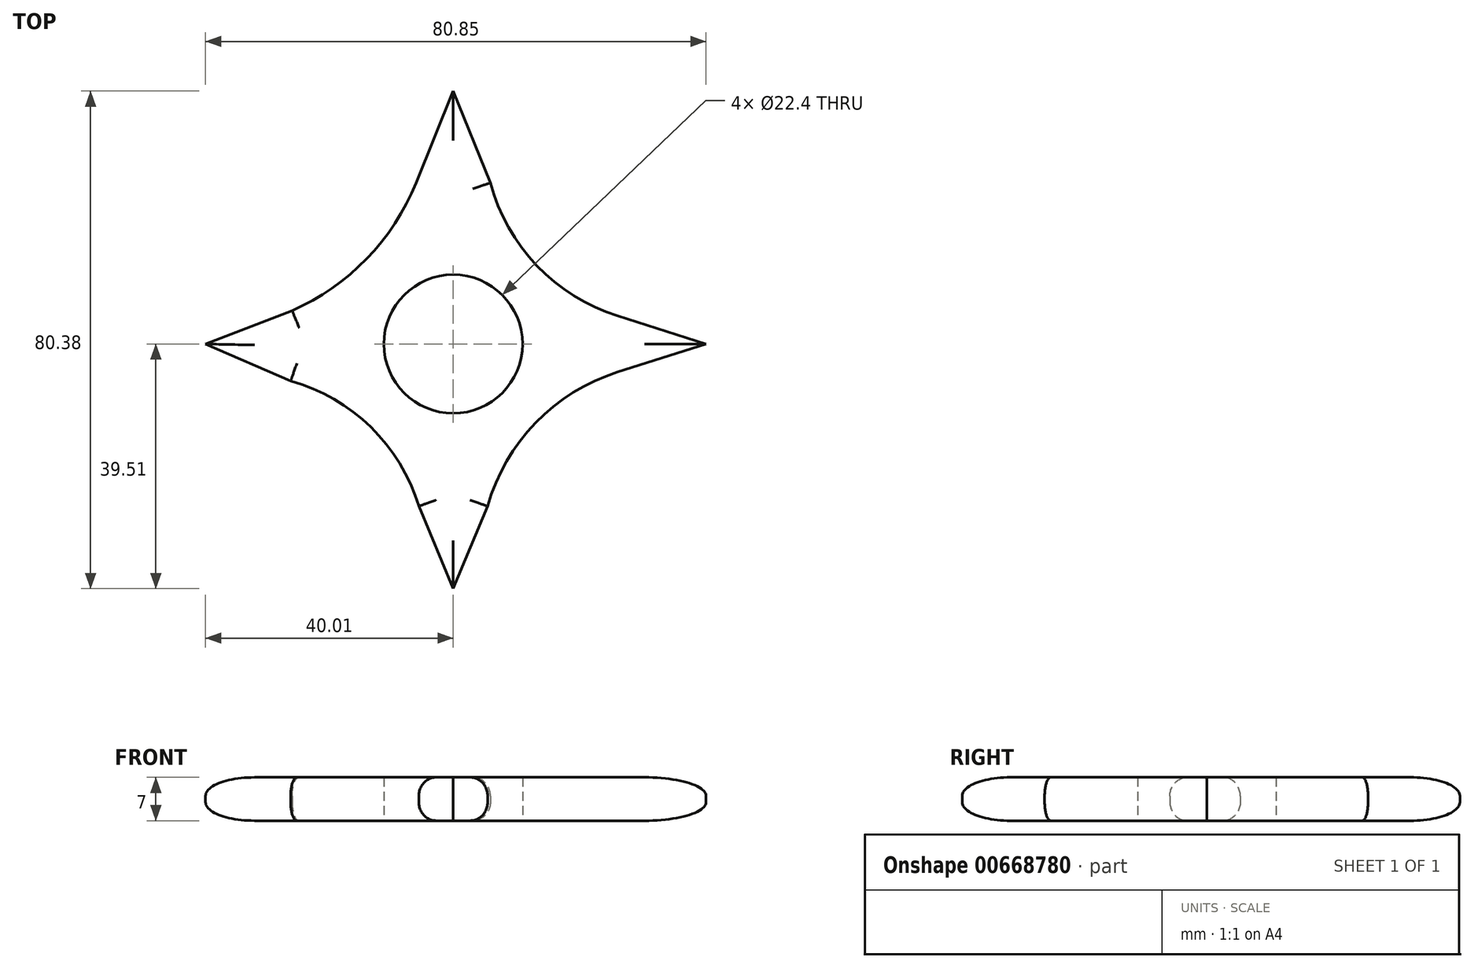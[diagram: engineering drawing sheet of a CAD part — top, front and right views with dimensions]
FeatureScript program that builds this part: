
annotation { "Feature Type Name" : "Feature", "Feature Type Description" : "" }
export const myFeature = defineFeature(function(context is Context, id is Id, definition is map)
    precondition{}
    {
        {
            var Q0;
            Q0=qCreatedBy(makeId("Top.planeOp"),FACE);
            var sketch = newSketch(context, id + "F0", { "sketchPlane" : qUnion([Q0])});
            skCircle(sketch, "E0", {"center": v(0, 0) * mm, "radius": 11.2 * mm});
            skLineSegment(sketch, "E1", {"start": v(0, 11.2) * mm, "end": v(0, 26.2) * mm});
            skLineSegment(sketch, "E2", {"start": v(11.2, 0) * mm, "end": v(26.2, 0) * mm});
            skLineSegment(sketch, "E3", {"start": v(0, -11.2) * mm, "end": v(0, -26.2) * mm});
            skLineSegment(sketch, "E4", {"start": v(-11.18, -0.6) * mm, "end": v(-26.17, 0) * mm});
            skLineSegment(sketch, "E5", {"start": v(0, -11.2) * mm, "end": v(5.57, -26.2) * mm});
            skLineSegment(sketch, "E6", {"start": v(0, -11.2) * mm, "end": v(-5.57, -26.2) * mm});
            skLineSegment(sketch, "E7", {"start": v(11.2, 0) * mm, "end": v(26.54, -4.54) * mm});
            skLineSegment(sketch, "E8", {"start": v(11.2, 0) * mm, "end": v(26.54, 4.54) * mm});
            skLineSegment(sketch, "E9", {"start": v(0, 11.2) * mm, "end": v(6, 26.03) * mm});
            skLineSegment(sketch, "E10", {"start": v(0, 11.2) * mm, "end": v(-6, 26.03) * mm});
            skLineSegment(sketch, "E11", {"start": v(-11.18, -0.6) * mm, "end": v(-26.02, 5.4) * mm});
            skLineSegment(sketch, "E12", {"start": v(-11.18, -0.6) * mm, "end": v(-26.25, -5.97) * mm});
            skLineSegment(sketch, "E13", {"start": v(-26.02, 5.4) * mm, "end": v(-40.01, 0) * mm});
            skLineSegment(sketch, "E14", {"start": v(-40.01, 0) * mm, "end": v(-26.25, -5.97) * mm});
            skLineSegment(sketch, "E15", {"start": v(-6, 26.03) * mm, "end": v(0, 40.87) * mm});
            skLineSegment(sketch, "E16", {"start": v(6, 26.03) * mm, "end": v(0, 40.87) * mm});
            skLineSegment(sketch, "E17", {"start": v(26.54, -4.54) * mm, "end": v(40.84, 0) * mm});
            skLineSegment(sketch, "E18", {"start": v(26.54, 4.54) * mm, "end": v(40.84, 0) * mm});
            skLineSegment(sketch, "E19", {"start": v(-5.57, -26.2) * mm, "end": v(0, -39.51) * mm});
            skLineSegment(sketch, "E20", {"start": v(0, -39.51) * mm, "end": v(5.57, -26.2) * mm});
            skPoint(sketch, "E21.visualSharp", {"position": v(6, 26.03) * mm});
            skLineSegment(sketch, "E21.filletArc", {"start": v(6, 26.03) * mm, "end": v(6, 26.03) * mm});
            skArc(sketch, "E22", {"start": v(6, 26.03) * mm, "mid": v(13.52, 12.66) * mm, "end": v(26.54, 4.54) * mm});
            skArc(sketch, "E23", {"start": v(-26.02, 5.4) * mm, "mid": v(-13.99, 13.76) * mm, "end": v(-6, 26.03) * mm});
            skArc(sketch, "E24", {"start": v(26.54, -4.54) * mm, "mid": v(13.32, -12.72) * mm, "end": v(5.57, -26.2) * mm});
            skArc(sketch, "E25", {"start": v(-5.57, -26.2) * mm, "mid": v(-13.31, -13.43) * mm, "end": v(-26.25, -5.97) * mm});
            skSolve(sketch);
        }
        {
            var Q0;
            Q0=qSketchRegion(id+"F0",true);
            extrude(context, id + "F1", {"entities" : qUnion([Q0]), "depth" : 7 * mm, "offsetDistance" : 25 * mm});
        }
        {
            var Q0;
            Q0=makeQuery(id+"F1.opExtrude","CAP_EDGE",EDGE,{"disambiguationData":[OSD([sQuery(id+"F0.wireOp",EDGE,"E23")])],"isStart":true});
            var Q1;
            Q1=makeQuery(id+"F1.opExtrude","CAP_EDGE",EDGE,{"disambiguationData":[OSD([sQuery(id+"F0.wireOp",EDGE,"E13")])],"isStart":true});
            var Q2;
            Q2=makeQuery(id+"F1.opExtrude","CAP_EDGE",EDGE,{"disambiguationData":[OSD([sQuery(id+"F0.wireOp",EDGE,"E14")])],"isStart":true});
            var Q3;
            Q3=makeQuery(id+"F1.opExtrude","CAP_EDGE",EDGE,{"disambiguationData":[OSD([sQuery(id+"F0.wireOp",EDGE,"E25")])],"isStart":true});
            var Q4;
            Q4=makeQuery(id+"F1.opExtrude","CAP_EDGE",EDGE,{"disambiguationData":[OSD([sQuery(id+"F0.wireOp",EDGE,"E20")])],"isStart":true});
            var Q5;
            Q5=makeQuery(id+"F1.opExtrude","CAP_EDGE",EDGE,{"disambiguationData":[OSD([sQuery(id+"F0.wireOp",EDGE,"E19")])],"isStart":true});
            var Q6;
            Q6=makeQuery(id+"F1.opExtrude","CAP_EDGE",EDGE,{"disambiguationData":[OSD([sQuery(id+"F0.wireOp",EDGE,"E24")])],"isStart":true});
            var Q7;
            Q7=makeQuery(id+"F1.opExtrude","CAP_EDGE",EDGE,{"disambiguationData":[OSD([sQuery(id+"F0.wireOp",EDGE,"E22")])],"isStart":true});
            var Q8;
            Q8=makeQuery(id+"F1.opExtrude","CAP_EDGE",EDGE,{"disambiguationData":[OSD([sQuery(id+"F0.wireOp",EDGE,"E16")])],"isStart":true});
            var Q9;
            Q9=makeQuery(id+"F1.opExtrude","CAP_EDGE",EDGE,{"disambiguationData":[OSD([sQuery(id+"F0.wireOp",EDGE,"E15")])],"isStart":true});
            var Q10;
            Q10=makeQuery(id+"F1.opExtrude","CAP_EDGE",EDGE,{"disambiguationData":[OSD([sQuery(id+"F0.wireOp",EDGE,"E18")])],"isStart":true});
            var Q11;
            Q11=makeQuery(id+"F1.opExtrude","CAP_EDGE",EDGE,{"disambiguationData":[OSD([sQuery(id+"F0.wireOp",EDGE,"E17")])],"isStart":true});
            fillet(context, id + "F2", {"entities" : qUnion([Q0, Q1, Q2, Q3, Q4, Q5, Q6, Q7, Q8, Q9, Q10, Q11]), "radius" : 3 * mm, "tangentPropagation" : true, "allowEdgeOverflow" : false});
        }
        {
            var Q0;
            Q0=makeQuery(id+"F1.opExtrude","CAP_EDGE",EDGE,{"disambiguationData":[OSD([sQuery(id+"F0.wireOp",EDGE,"E22")])],"isStart":false});
            var Q1;
            Q1=makeQuery(id+"F1.opExtrude","CAP_EDGE",EDGE,{"disambiguationData":[OSD([sQuery(id+"F0.wireOp",EDGE,"E23")])],"isStart":false});
            var Q2;
            Q2=makeQuery(id+"F1.opExtrude","CAP_EDGE",EDGE,{"disambiguationData":[OSD([sQuery(id+"F0.wireOp",EDGE,"E25")])],"isStart":false});
            var Q3;
            Q3=makeQuery(id+"F1.opExtrude","CAP_EDGE",EDGE,{"disambiguationData":[OSD([sQuery(id+"F0.wireOp",EDGE,"E24")])],"isStart":false});
            var Q4;
            Q4=makeQuery(id+"F1.opExtrude","CAP_EDGE",EDGE,{"disambiguationData":[OSD([sQuery(id+"F0.wireOp",EDGE,"E20")])],"isStart":false});
            var Q5;
            Q5=makeQuery(id+"F1.opExtrude","CAP_EDGE",EDGE,{"disambiguationData":[OSD([sQuery(id+"F0.wireOp",EDGE,"E19")])],"isStart":false});
            var Q6;
            Q6=makeQuery(id+"F1.opExtrude","CAP_EDGE",EDGE,{"disambiguationData":[OSD([sQuery(id+"F0.wireOp",EDGE,"E17")])],"isStart":false});
            var Q7;
            Q7=makeQuery(id+"F1.opExtrude","CAP_EDGE",EDGE,{"disambiguationData":[OSD([sQuery(id+"F0.wireOp",EDGE,"E18")])],"isStart":false});
            var Q8;
            Q8=makeQuery(id+"F1.opExtrude","CAP_EDGE",EDGE,{"disambiguationData":[OSD([sQuery(id+"F0.wireOp",EDGE,"E15")])],"isStart":false});
            var Q9;
            Q9=makeQuery(id+"F1.opExtrude","CAP_EDGE",EDGE,{"disambiguationData":[OSD([sQuery(id+"F0.wireOp",EDGE,"E16")])],"isStart":false});
            var Q10;
            Q10=makeQuery(id+"F1.opExtrude","CAP_EDGE",EDGE,{"disambiguationData":[OSD([sQuery(id+"F0.wireOp",EDGE,"E13")])],"isStart":false});
            var Q11;
            Q11=makeQuery(id+"F1.opExtrude","CAP_EDGE",EDGE,{"disambiguationData":[OSD([sQuery(id+"F0.wireOp",EDGE,"E14")])],"isStart":false});
            fillet(context, id + "F3", {"entities" : qUnion([Q0, Q1, Q2, Q3, Q4, Q5, Q6, Q7, Q8, Q9, Q10, Q11]), "radius" : 3 * mm, "tangentPropagation" : true, "allowEdgeOverflow" : false});
        }
    });
